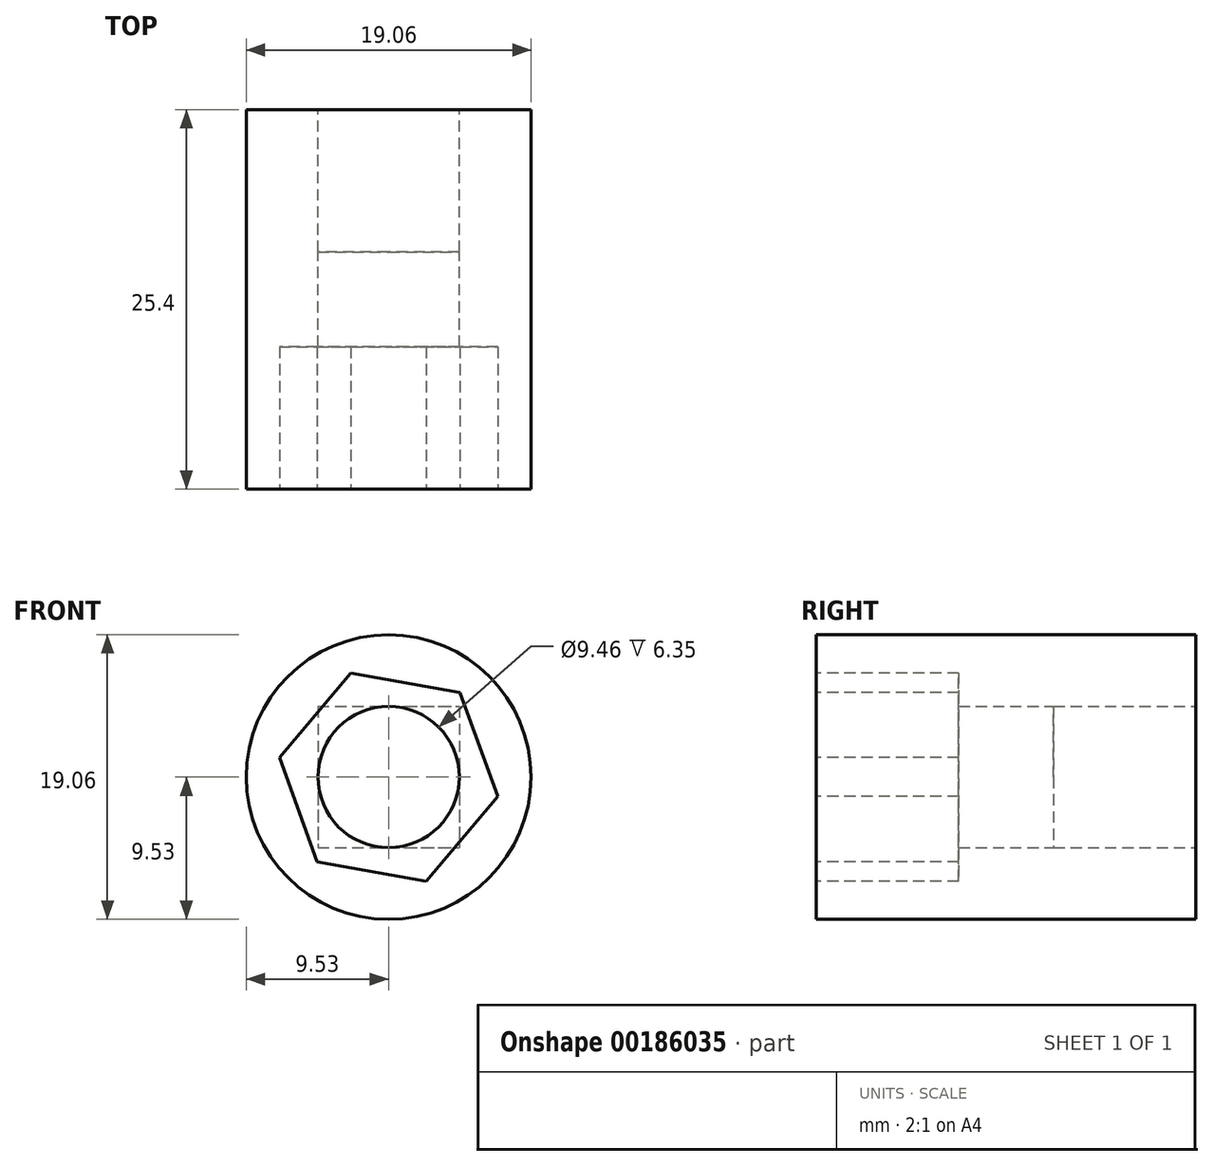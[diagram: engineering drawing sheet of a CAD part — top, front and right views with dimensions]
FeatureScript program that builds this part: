
annotation { "Feature Type Name" : "Feature", "Feature Type Description" : "" }
export const myFeature = defineFeature(function(context is Context, id is Id, definition is map)
    precondition{}
    {
        {
            var Q0;
            Q0=qCreatedBy(makeId("Front.planeOp"),FACE);
            var sketch = newSketch(context, id + "F0", { "sketchPlane" : qUnion([Q0])});
            skCircle(sketch, "E0", {"center": v(0, 0) * mm, "radius": 9.53 * mm});
            skSolve(sketch);
        }
        {
            var Q0;
            Q0=qCreatedBy(makeId("Front.planeOp"),FACE);
            var sketch = newSketch(context, id + "F1", { "sketchPlane" : qUnion([Q0])});
            skLineSegment(sketch, "E1.bottom", {"start": v(-4.73, 4.73) * mm, "end": v(4.73, 4.73) * mm});
            skLineSegment(sketch, "E1.top", {"start": v(-4.73, -4.73) * mm, "end": v(4.73, -4.73) * mm});
            skLineSegment(sketch, "E1.left", {"start": v(-4.73, 4.73) * mm, "end": v(-4.73, -4.73) * mm});
            skLineSegment(sketch, "E1.right", {"start": v(4.73, 4.73) * mm, "end": v(4.73, -4.73) * mm});
            skPoint(sketch, "E1.middle", {"position": v(0, 0) * mm});
            skCircle(sketch, "E2", {"center": v(0, 0) * mm, "radius": 4.73 * mm});
            skSolve(sketch);
        }
        {
            var Q0;
            Q0=makeQuery(id+"F0.imprint","IMPRINT",FACE,{"disambiguationData":[TD([[makeQuery(id+"F0.imprint","IMPRINT",EDGE,{"derivedFrom":sQuery(id+"F0.wireOp",EDGE,"E0")}),1.0]])]});
            extrude(context, id + "F2", {"entities" : qUnion([Q0]), "depth" : 25.4 * mm});
        }
        {
            var Q0;
            {var subQ0=sQuery(id+"F1.wireOp",EDGE,"E2");var subQ1=makeQuery(id+"F1.imprint","INTERSECT",VERTEX,{"derivedFrom":[sQuery(id+"F1.wireOp",EDGE,"E1.bottom"),subQ0]});Q0=makeQuery(id+"F1.imprint","IMPRINT",FACE,{"disambiguationData":[TD([[makeQuery(id+"F1.imprint","IMPRINT",EDGE,{"disambiguationData":[TD([[subQ1,1.0]])],"derivedFrom":subQ0}),1.0]])]});}
            extrude(context, id + "F3", {"entities" : qUnion([Q0]), "operationType" : NewBodyOperationType.REMOVE, "endBound" : BoundingType.THROUGH_ALL, "depth" : 25.4 * mm});
        }
        {
            var Q0;
            Q0 = qSketchRegion(id + "F1", true);
            extrude(context, id + "F4", {"entities" : qUnion([Q0]), "operationType" : NewBodyOperationType.REMOVE, "depth" : 9.52 * mm});
        }
        {
            var Q0;
            Q0=makeQuery(id+"F2.opExtrude","CAP_FACE",FACE,{"disambiguationData":[OSD([sQuery(id+"F0.wireOp",EDGE,"E0")])],"isStart":false});
            var sketch = newSketch(context, id + "F5", { "sketchPlane" : qUnion([Q0])});
            skCircle(sketch, "E3.cCircle", {"center": v(0, 0) * mm, "radius": 6.42 * mm, "construction": true});
            skLineSegment(sketch, "E3.0", {"start": v(4.78, 5.67) * mm, "end": v(7.3, -1.3) * mm});
            skLineSegment(sketch, "E3.1", {"start": v(7.3, -1.3) * mm, "end": v(2.52, -6.98) * mm});
            skLineSegment(sketch, "E3.2", {"start": v(2.52, -6.98) * mm, "end": v(-4.78, -5.67) * mm});
            skLineSegment(sketch, "E3.3", {"start": v(-4.78, -5.67) * mm, "end": v(-7.3, 1.3) * mm});
            skLineSegment(sketch, "E3.4", {"start": v(-7.3, 1.3) * mm, "end": v(-2.52, 6.98) * mm});
            skLineSegment(sketch, "E3.5", {"start": v(-2.52, 6.98) * mm, "end": v(4.78, 5.67) * mm});
            skPoint(sketch, "E3.0.midPoint", {"position": v(6.04, 2.19) * mm});
            skSolve(sketch);
        }
        {
            var Q0;
            Q0=makeQuery(id+"F5.imprint","IMPRINT",FACE,{"disambiguationData":[TD([[makeQuery(id+"F5.imprint","IMPRINT",EDGE,{"derivedFrom":sQuery(id+"F5.wireOp",EDGE,"E3.0")}),-1.0]])]});
            extrude(context, id + "F6", {"entities" : qUnion([Q0]), "operationType" : NewBodyOperationType.REMOVE, "oppositeDirection" : true, "depth" : 9.52 * mm});
        }
    });
